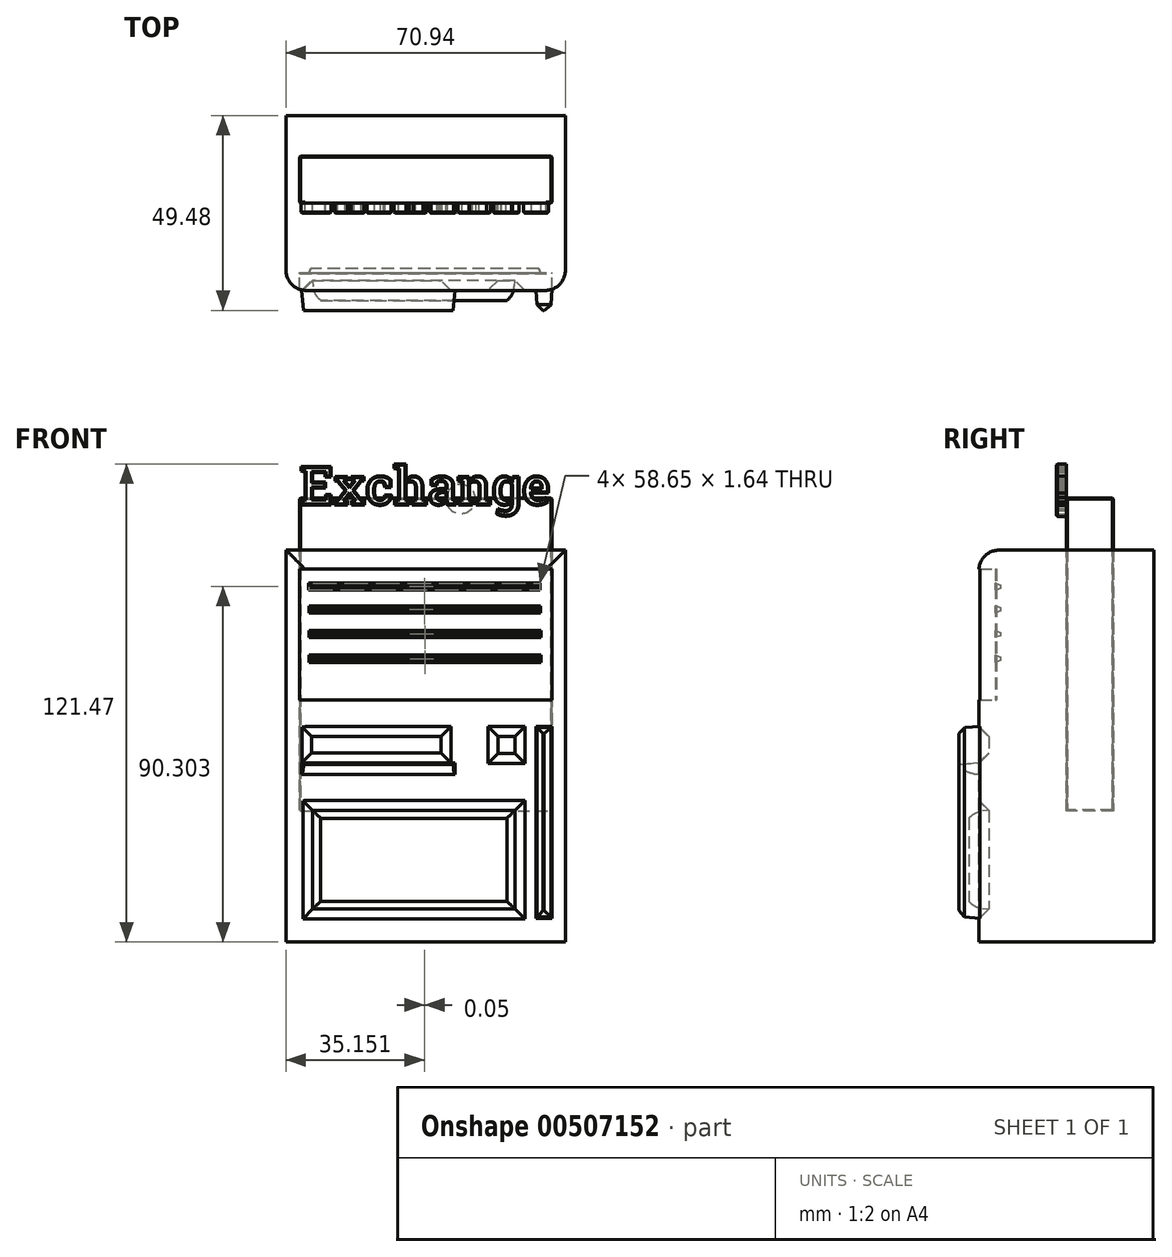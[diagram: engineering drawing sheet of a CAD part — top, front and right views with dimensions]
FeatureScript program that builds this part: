
annotation { "Feature Type Name" : "Feature", "Feature Type Description" : "" }
export const myFeature = defineFeature(function(context is Context, id is Id, definition is map)
    precondition{}
    {
        {
            var Q0;
            Q0=qCreatedBy(makeId("Top.planeOp"),FACE);
            var sketch = newSketch(context, id + "F0", { "sketchPlane" : qUnion([Q0])});
            skLineSegment(sketch, "E0.bottom", {"start": v(35.47, 22.2) * mm, "end": v(-35.47, 22.2) * mm});
            skLineSegment(sketch, "E0.top", {"start": v(35.47, -22.2) * mm, "end": v(-35.47, -22.2) * mm});
            skLineSegment(sketch, "E0.left", {"start": v(35.47, 22.2) * mm, "end": v(35.47, -22.2) * mm});
            skLineSegment(sketch, "E0.right", {"start": v(-35.47, 22.2) * mm, "end": v(-35.47, -22.2) * mm});
            skPoint(sketch, "E0.middle", {"position": v(0, 0) * mm});
            skLineSegment(sketch, "E1.bottom", {"start": v(-32.06, -22.2) * mm, "end": v(32.06, -22.2) * mm});
            skLineSegment(sketch, "E1.top", {"start": v(-32.06, -17.74) * mm, "end": v(32.06, -17.74) * mm});
            skLineSegment(sketch, "E1.left", {"start": v(-32.06, -22.2) * mm, "end": v(-32.06, -17.74) * mm});
            skLineSegment(sketch, "E1.right", {"start": v(32.06, -22.2) * mm, "end": v(32.06, -17.74) * mm});
            skLineSegment(sketch, "E2.bottom", {"start": v(32.06, -22.2) * mm, "end": v(-32.06, -22.2) * mm});
            skLineSegment(sketch, "E2.top", {"start": v(32.06, -31.14) * mm, "end": v(-32.06, -31.14) * mm});
            skLineSegment(sketch, "E2.left", {"start": v(32.06, -22.2) * mm, "end": v(32.06, -31.14) * mm});
            skLineSegment(sketch, "E2.right", {"start": v(-32.06, -22.2) * mm, "end": v(-32.06, -31.14) * mm});
            skLineSegment(sketch, "E3.bottom", {"start": v(-32.06, 22.2) * mm, "end": v(32.06, 22.2) * mm});
            skLineSegment(sketch, "E3.top", {"start": v(-32.06, 26.14) * mm, "end": v(32.06, 26.14) * mm});
            skLineSegment(sketch, "E3.left", {"start": v(-32.06, 22.2) * mm, "end": v(-32.06, 26.14) * mm});
            skLineSegment(sketch, "E3.right", {"start": v(32.06, 22.2) * mm, "end": v(32.06, 26.14) * mm});
            skLineSegment(sketch, "E4.bottom", {"start": v(-32.06, 0) * mm, "end": v(32.06, 0) * mm});
            skLineSegment(sketch, "E4.top", {"start": v(-32.06, 11.96) * mm, "end": v(32.06, 11.96) * mm});
            skLineSegment(sketch, "E4.left", {"start": v(-32.06, 0) * mm, "end": v(-32.06, 11.96) * mm});
            skLineSegment(sketch, "E4.right", {"start": v(32.06, 0) * mm, "end": v(32.06, 11.96) * mm});
            skSolve(sketch);
        }
        {
            var Q0;
            Q0=makeQuery(id+"F0.imprint","IMPRINT",FACE,{"disambiguationData":[TD([[makeQuery(id+"F0.imprint","IMPRINT",EDGE,{"derivedFrom":sQuery(id+"F0.wireOp",EDGE,"E4.bottom")}),1.0]])]});
            var Q1;
            {var subQ3=sQuery(id+"F0.wireOp",EDGE,"E0.left");Q1=makeQuery(id+"F0.imprint","IMPRINT",FACE,{"disambiguationData":[TD([[makeQuery(id+"F0.imprint","IMPRINT",EDGE,{"derivedFrom":subQ3}),-1.0]])]});}
            var Q2;
            Q2=makeQuery(id+"F0.imprint","IMPRINT",FACE,{"disambiguationData":[TD([[makeQuery(id+"F0.imprint","IMPRINT",EDGE,{"derivedFrom":sQuery(id+"F0.wireOp",EDGE,"E1.top")}),-1.0]])]});
            var Q3;
            Q3=makeQuery(id+"F0.imprint","IMPRINT",FACE,{"disambiguationData":[TD([[makeQuery(id+"F0.imprint","IMPRINT",EDGE,{"derivedFrom":sQuery(id+"F0.wireOp",EDGE,"E3.bottom")}),1.0]])]});
            extrude(context, id + "F1", {"entities" : qUnion([Q0, Q1, Q2, Q3]), "depth" : 99.57 * mm});
        }
        {
            var Q0;
            Q0=makeQuery(id+"F0.imprint","IMPRINT",FACE,{"disambiguationData":[TD([[makeQuery(id+"F0.imprint","IMPRINT",EDGE,{"derivedFrom":sQuery(id+"F0.wireOp",EDGE,"E1.top")}),-1.0]])]});
            extrude(context, id + "F2", {"entities" : qUnion([Q0]), "operationType" : NewBodyOperationType.REMOVE, "depth" : 94.74 * mm, "hasSecondDirection" : true, "secondDirectionOppositeDirection" : false, "secondDirectionDepth" : 61.47 * mm});
        }
        {
            var Q0;
            Q0=makeQuery(id+"F2.boolean.opBoolean","COPY",FACE,{"derivedFrom":makeQuery(id+"F2.opExtrude","SWEPT_FACE",FACE,{"disambiguationData":[OSD([sQuery(id+"F0.wireOp",EDGE,"E1.top")])]})});
            extrude(context, id + "F3", {"entities" : qUnion([Q0]), "depth" : 0.25 * mm});
        }
        {
            var Q0;
            Q0=makeQuery(id+"F0.imprint","IMPRINT",FACE,{"disambiguationData":[TD([[makeQuery(id+"F0.imprint","IMPRINT",EDGE,{"derivedFrom":sQuery(id+"F0.wireOp",EDGE,"E4.bottom")}),1.0]])]});
            extrude(context, id + "F4", {"entities" : qUnion([Q0]), "depth" : 112.78 * mm, "hasSecondDirection" : true, "secondDirectionOppositeDirection" : false, "secondDirectionDepth" : 33.27 * mm});
        }
        {
            var Q0;
            Q0=makeQuery(id+"F4.opExtrude","SWEPT_FACE",FACE,{"disambiguationData":[OSD([sQuery(id+"F0.wireOp",EDGE,"E4.bottom")])]});
            var sketch = newSketch(context, id + "F5", { "sketchPlane" : qUnion([Q0])});
            skText(sketch, "E5", { "text": "Exchange", "fontName": "RobotoSlab-Bold.ttf"});
            const initialGuessF5  = {"E5": [-0.03206, 0.11107, 1, 0, 0.00983]};
            skSetInitialGuess(sketch, initialGuessF5);
            skSolve(sketch);
        }
        {
            var Q0;
            Q0 = qSketchRegion(id + "F5", true);
            extrude(context, id + "F6", {"entities" : qUnion([Q0]), "operationType" : NewBodyOperationType.ADD, "depth" : 2.54 * mm});
        }
        {
            var Q0;
            Q0=makeQuery(id+"F6.opExtrude","CAP_FACE",FACE,{"disambiguationData":[OSD([sQuery(id+"F5.wireOp",EDGE,"E5.sketch_text.stroke-0"),sQuery(id+"F5.wireOp",EDGE,"E5.sketch_text.stroke-1"),sQuery(id+"F5.wireOp",EDGE,"E5.sketch_text.stroke-2"),sQuery(id+"F5.wireOp",EDGE,"E5.sketch_text.stroke-3"),sQuery(id+"F5.wireOp",EDGE,"E5.sketch_text.stroke-4"),sQuery(id+"F5.wireOp",EDGE,"E5.sketch_text.stroke-5"),sQuery(id+"F5.wireOp",EDGE,"E5.sketch_text.stroke-6"),sQuery(id+"F5.wireOp",EDGE,"E5.sketch_text.stroke-7"),sQuery(id+"F5.wireOp",EDGE,"E5.sketch_text.stroke-8"),sQuery(id+"F5.wireOp",EDGE,"E5.sketch_text.stroke-9"),sQuery(id+"F5.wireOp",EDGE,"E5.sketch_text.stroke-10"),sQuery(id+"F5.wireOp",EDGE,"E5.sketch_text.stroke-11"),sQuery(id+"F5.wireOp",EDGE,"E5.sketch_text.stroke-12"),sQuery(id+"F5.wireOp",EDGE,"E5.sketch_text.stroke-13"),sQuery(id+"F5.wireOp",EDGE,"E5.sketch_text.stroke-14"),sQuery(id+"F5.wireOp",EDGE,"E5.sketch_text.stroke-15"),sQuery(id+"F5.wireOp",EDGE,"E5.sketch_text.stroke-16"),sQuery(id+"F5.wireOp",EDGE,"E5.sketch_text.stroke-17"),sQuery(id+"F5.wireOp",EDGE,"E5.sketch_text.stroke-18"),sQuery(id+"F5.wireOp",EDGE,"E5.sketch_text.stroke-19"),sQuery(id+"F5.wireOp",EDGE,"E5.sketch_text.stroke-20")])],"isStart":false});
            var Q1;
            Q1=makeQuery(id+"F6.opExtrude","CAP_FACE",FACE,{"disambiguationData":[OSD([sQuery(id+"F5.wireOp",EDGE,"E5.sketch_text.stroke-21"),sQuery(id+"F5.wireOp",EDGE,"E5.sketch_text.stroke-22"),sQuery(id+"F5.wireOp",EDGE,"E5.sketch_text.stroke-23"),sQuery(id+"F5.wireOp",EDGE,"E5.sketch_text.stroke-24"),sQuery(id+"F5.wireOp",EDGE,"E5.sketch_text.stroke-25"),sQuery(id+"F5.wireOp",EDGE,"E5.sketch_text.stroke-26"),sQuery(id+"F5.wireOp",EDGE,"E5.sketch_text.stroke-27"),sQuery(id+"F5.wireOp",EDGE,"E5.sketch_text.stroke-28"),sQuery(id+"F5.wireOp",EDGE,"E5.sketch_text.stroke-29"),sQuery(id+"F5.wireOp",EDGE,"E5.sketch_text.stroke-30"),sQuery(id+"F5.wireOp",EDGE,"E5.sketch_text.stroke-31"),sQuery(id+"F5.wireOp",EDGE,"E5.sketch_text.stroke-32"),sQuery(id+"F5.wireOp",EDGE,"E5.sketch_text.stroke-33"),sQuery(id+"F5.wireOp",EDGE,"E5.sketch_text.stroke-34"),sQuery(id+"F5.wireOp",EDGE,"E5.sketch_text.stroke-35"),sQuery(id+"F5.wireOp",EDGE,"E5.sketch_text.stroke-36"),sQuery(id+"F5.wireOp",EDGE,"E5.sketch_text.stroke-37"),sQuery(id+"F5.wireOp",EDGE,"E5.sketch_text.stroke-38"),sQuery(id+"F5.wireOp",EDGE,"E5.sketch_text.stroke-39"),sQuery(id+"F5.wireOp",EDGE,"E5.sketch_text.stroke-40"),sQuery(id+"F5.wireOp",EDGE,"E5.sketch_text.stroke-41"),sQuery(id+"F5.wireOp",EDGE,"E5.sketch_text.stroke-42"),sQuery(id+"F5.wireOp",EDGE,"E5.sketch_text.stroke-43"),sQuery(id+"F5.wireOp",EDGE,"E5.sketch_text.stroke-44"),sQuery(id+"F5.wireOp",EDGE,"E5.sketch_text.stroke-45"),sQuery(id+"F5.wireOp",EDGE,"E5.sketch_text.stroke-46"),sQuery(id+"F5.wireOp",EDGE,"E5.sketch_text.stroke-47"),sQuery(id+"F5.wireOp",EDGE,"E5.sketch_text.stroke-48")])],"isStart":false});
            var Q2;
            Q2=makeQuery(id+"F6.opExtrude","CAP_FACE",FACE,{"disambiguationData":[OSD([sQuery(id+"F5.wireOp",EDGE,"E5.sketch_text.stroke-49"),sQuery(id+"F5.wireOp",EDGE,"E5.sketch_text.stroke-50"),sQuery(id+"F5.wireOp",EDGE,"E5.sketch_text.stroke-51"),sQuery(id+"F5.wireOp",EDGE,"E5.sketch_text.stroke-52"),sQuery(id+"F5.wireOp",EDGE,"E5.sketch_text.stroke-53"),sQuery(id+"F5.wireOp",EDGE,"E5.sketch_text.stroke-54"),sQuery(id+"F5.wireOp",EDGE,"E5.sketch_text.stroke-55"),sQuery(id+"F5.wireOp",EDGE,"E5.sketch_text.stroke-56"),sQuery(id+"F5.wireOp",EDGE,"E5.sketch_text.stroke-57"),sQuery(id+"F5.wireOp",EDGE,"E5.sketch_text.stroke-58"),sQuery(id+"F5.wireOp",EDGE,"E5.sketch_text.stroke-59"),sQuery(id+"F5.wireOp",EDGE,"E5.sketch_text.stroke-60"),sQuery(id+"F5.wireOp",EDGE,"E5.sketch_text.stroke-61"),sQuery(id+"F5.wireOp",EDGE,"E5.sketch_text.stroke-62"),sQuery(id+"F5.wireOp",EDGE,"E5.sketch_text.stroke-63"),sQuery(id+"F5.wireOp",EDGE,"E5.sketch_text.stroke-64"),sQuery(id+"F5.wireOp",EDGE,"E5.sketch_text.stroke-65"),sQuery(id+"F5.wireOp",EDGE,"E5.sketch_text.stroke-66"),sQuery(id+"F5.wireOp",EDGE,"E5.sketch_text.stroke-67"),sQuery(id+"F5.wireOp",EDGE,"E5.sketch_text.stroke-68"),sQuery(id+"F5.wireOp",EDGE,"E5.sketch_text.stroke-69"),sQuery(id+"F5.wireOp",EDGE,"E5.sketch_text.stroke-70"),sQuery(id+"F5.wireOp",EDGE,"E5.sketch_text.stroke-71")])],"isStart":false});
            var Q3;
            Q3=makeQuery(id+"F6.opExtrude","CAP_FACE",FACE,{"disambiguationData":[OSD([sQuery(id+"F5.wireOp",EDGE,"E5.sketch_text.stroke-72"),sQuery(id+"F5.wireOp",EDGE,"E5.sketch_text.stroke-73"),sQuery(id+"F5.wireOp",EDGE,"E5.sketch_text.stroke-74"),sQuery(id+"F5.wireOp",EDGE,"E5.sketch_text.stroke-75"),sQuery(id+"F5.wireOp",EDGE,"E5.sketch_text.stroke-76"),sQuery(id+"F5.wireOp",EDGE,"E5.sketch_text.stroke-77"),sQuery(id+"F5.wireOp",EDGE,"E5.sketch_text.stroke-78"),sQuery(id+"F5.wireOp",EDGE,"E5.sketch_text.stroke-79"),sQuery(id+"F5.wireOp",EDGE,"E5.sketch_text.stroke-80"),sQuery(id+"F5.wireOp",EDGE,"E5.sketch_text.stroke-81"),sQuery(id+"F5.wireOp",EDGE,"E5.sketch_text.stroke-82"),sQuery(id+"F5.wireOp",EDGE,"E5.sketch_text.stroke-83"),sQuery(id+"F5.wireOp",EDGE,"E5.sketch_text.stroke-84"),sQuery(id+"F5.wireOp",EDGE,"E5.sketch_text.stroke-85"),sQuery(id+"F5.wireOp",EDGE,"E5.sketch_text.stroke-86"),sQuery(id+"F5.wireOp",EDGE,"E5.sketch_text.stroke-87"),sQuery(id+"F5.wireOp",EDGE,"E5.sketch_text.stroke-88"),sQuery(id+"F5.wireOp",EDGE,"E5.sketch_text.stroke-89"),sQuery(id+"F5.wireOp",EDGE,"E5.sketch_text.stroke-90"),sQuery(id+"F5.wireOp",EDGE,"E5.sketch_text.stroke-91"),sQuery(id+"F5.wireOp",EDGE,"E5.sketch_text.stroke-92"),sQuery(id+"F5.wireOp",EDGE,"E5.sketch_text.stroke-93"),sQuery(id+"F5.wireOp",EDGE,"E5.sketch_text.stroke-94"),sQuery(id+"F5.wireOp",EDGE,"E5.sketch_text.stroke-95"),sQuery(id+"F5.wireOp",EDGE,"E5.sketch_text.stroke-96"),sQuery(id+"F5.wireOp",EDGE,"E5.sketch_text.stroke-97")])],"isStart":false});
            var Q4;
            Q4=makeQuery(id+"F6.opExtrude","CAP_FACE",FACE,{"disambiguationData":[OSD([sQuery(id+"F5.wireOp",EDGE,"E5.sketch_text.stroke-98"),sQuery(id+"F5.wireOp",EDGE,"E5.sketch_text.stroke-99"),sQuery(id+"F5.wireOp",EDGE,"E5.sketch_text.stroke-100"),sQuery(id+"F5.wireOp",EDGE,"E5.sketch_text.stroke-101"),sQuery(id+"F5.wireOp",EDGE,"E5.sketch_text.stroke-102"),sQuery(id+"F5.wireOp",EDGE,"E5.sketch_text.stroke-103"),sQuery(id+"F5.wireOp",EDGE,"E5.sketch_text.stroke-104"),sQuery(id+"F5.wireOp",EDGE,"E5.sketch_text.stroke-105"),sQuery(id+"F5.wireOp",EDGE,"E5.sketch_text.stroke-106"),sQuery(id+"F5.wireOp",EDGE,"E5.sketch_text.stroke-107"),sQuery(id+"F5.wireOp",EDGE,"E5.sketch_text.stroke-108"),sQuery(id+"F5.wireOp",EDGE,"E5.sketch_text.stroke-109"),sQuery(id+"F5.wireOp",EDGE,"E5.sketch_text.stroke-110"),sQuery(id+"F5.wireOp",EDGE,"E5.sketch_text.stroke-111"),sQuery(id+"F5.wireOp",EDGE,"E5.sketch_text.stroke-112"),sQuery(id+"F5.wireOp",EDGE,"E5.sketch_text.stroke-113"),sQuery(id+"F5.wireOp",EDGE,"E5.sketch_text.stroke-114"),sQuery(id+"F5.wireOp",EDGE,"E5.sketch_text.stroke-115"),sQuery(id+"F5.wireOp",EDGE,"E5.sketch_text.stroke-116"),sQuery(id+"F5.wireOp",EDGE,"E5.sketch_text.stroke-117"),sQuery(id+"F5.wireOp",EDGE,"E5.sketch_text.stroke-118"),sQuery(id+"F5.wireOp",EDGE,"E5.sketch_text.stroke-119"),sQuery(id+"F5.wireOp",EDGE,"E5.sketch_text.stroke-120"),sQuery(id+"F5.wireOp",EDGE,"E5.sketch_text.stroke-121"),sQuery(id+"F5.wireOp",EDGE,"E5.sketch_text.stroke-122"),sQuery(id+"F5.wireOp",EDGE,"E5.sketch_text.stroke-123"),sQuery(id+"F5.wireOp",EDGE,"E5.sketch_text.stroke-124"),sQuery(id+"F5.wireOp",EDGE,"E5.sketch_text.stroke-125"),sQuery(id+"F5.wireOp",EDGE,"E5.sketch_text.stroke-126"),sQuery(id+"F5.wireOp",EDGE,"E5.sketch_text.stroke-127"),sQuery(id+"F5.wireOp",EDGE,"E5.sketch_text.stroke-128"),sQuery(id+"F5.wireOp",EDGE,"E5.sketch_text.stroke-129"),sQuery(id+"F5.wireOp",EDGE,"E5.sketch_text.stroke-130"),sQuery(id+"F5.wireOp",EDGE,"E5.sketch_text.stroke-131"),sQuery(id+"F5.wireOp",EDGE,"E5.sketch_text.stroke-132")])],"isStart":false});
            var Q5;
            Q5=makeQuery(id+"F6.opExtrude","CAP_FACE",FACE,{"disambiguationData":[OSD([sQuery(id+"F5.wireOp",EDGE,"E5.sketch_text.stroke-133"),sQuery(id+"F5.wireOp",EDGE,"E5.sketch_text.stroke-134"),sQuery(id+"F5.wireOp",EDGE,"E5.sketch_text.stroke-135"),sQuery(id+"F5.wireOp",EDGE,"E5.sketch_text.stroke-136"),sQuery(id+"F5.wireOp",EDGE,"E5.sketch_text.stroke-137"),sQuery(id+"F5.wireOp",EDGE,"E5.sketch_text.stroke-138"),sQuery(id+"F5.wireOp",EDGE,"E5.sketch_text.stroke-139"),sQuery(id+"F5.wireOp",EDGE,"E5.sketch_text.stroke-140"),sQuery(id+"F5.wireOp",EDGE,"E5.sketch_text.stroke-141"),sQuery(id+"F5.wireOp",EDGE,"E5.sketch_text.stroke-142"),sQuery(id+"F5.wireOp",EDGE,"E5.sketch_text.stroke-143"),sQuery(id+"F5.wireOp",EDGE,"E5.sketch_text.stroke-144"),sQuery(id+"F5.wireOp",EDGE,"E5.sketch_text.stroke-145"),sQuery(id+"F5.wireOp",EDGE,"E5.sketch_text.stroke-146"),sQuery(id+"F5.wireOp",EDGE,"E5.sketch_text.stroke-147"),sQuery(id+"F5.wireOp",EDGE,"E5.sketch_text.stroke-148"),sQuery(id+"F5.wireOp",EDGE,"E5.sketch_text.stroke-149"),sQuery(id+"F5.wireOp",EDGE,"E5.sketch_text.stroke-150"),sQuery(id+"F5.wireOp",EDGE,"E5.sketch_text.stroke-151"),sQuery(id+"F5.wireOp",EDGE,"E5.sketch_text.stroke-152"),sQuery(id+"F5.wireOp",EDGE,"E5.sketch_text.stroke-153"),sQuery(id+"F5.wireOp",EDGE,"E5.sketch_text.stroke-154"),sQuery(id+"F5.wireOp",EDGE,"E5.sketch_text.stroke-155"),sQuery(id+"F5.wireOp",EDGE,"E5.sketch_text.stroke-156"),sQuery(id+"F5.wireOp",EDGE,"E5.sketch_text.stroke-157"),sQuery(id+"F5.wireOp",EDGE,"E5.sketch_text.stroke-158")])],"isStart":false});
            var Q6;
            Q6=makeQuery(id+"F6.opExtrude","CAP_FACE",FACE,{"disambiguationData":[OSD([sQuery(id+"F5.wireOp",EDGE,"E5.sketch_text.stroke-159"),sQuery(id+"F5.wireOp",EDGE,"E5.sketch_text.stroke-160"),sQuery(id+"F5.wireOp",EDGE,"E5.sketch_text.stroke-161"),sQuery(id+"F5.wireOp",EDGE,"E5.sketch_text.stroke-162"),sQuery(id+"F5.wireOp",EDGE,"E5.sketch_text.stroke-163"),sQuery(id+"F5.wireOp",EDGE,"E5.sketch_text.stroke-164"),sQuery(id+"F5.wireOp",EDGE,"E5.sketch_text.stroke-165"),sQuery(id+"F5.wireOp",EDGE,"E5.sketch_text.stroke-166"),sQuery(id+"F5.wireOp",EDGE,"E5.sketch_text.stroke-167"),sQuery(id+"F5.wireOp",EDGE,"E5.sketch_text.stroke-168"),sQuery(id+"F5.wireOp",EDGE,"E5.sketch_text.stroke-169"),sQuery(id+"F5.wireOp",EDGE,"E5.sketch_text.stroke-170"),sQuery(id+"F5.wireOp",EDGE,"E5.sketch_text.stroke-171"),sQuery(id+"F5.wireOp",EDGE,"E5.sketch_text.stroke-172"),sQuery(id+"F5.wireOp",EDGE,"E5.sketch_text.stroke-173"),sQuery(id+"F5.wireOp",EDGE,"E5.sketch_text.stroke-174"),sQuery(id+"F5.wireOp",EDGE,"E5.sketch_text.stroke-175"),sQuery(id+"F5.wireOp",EDGE,"E5.sketch_text.stroke-176"),sQuery(id+"F5.wireOp",EDGE,"E5.sketch_text.stroke-177"),sQuery(id+"F5.wireOp",EDGE,"E5.sketch_text.stroke-178"),sQuery(id+"F5.wireOp",EDGE,"E5.sketch_text.stroke-179"),sQuery(id+"F5.wireOp",EDGE,"E5.sketch_text.stroke-180"),sQuery(id+"F5.wireOp",EDGE,"E5.sketch_text.stroke-181"),sQuery(id+"F5.wireOp",EDGE,"E5.sketch_text.stroke-182"),sQuery(id+"F5.wireOp",EDGE,"E5.sketch_text.stroke-183"),sQuery(id+"F5.wireOp",EDGE,"E5.sketch_text.stroke-184"),sQuery(id+"F5.wireOp",EDGE,"E5.sketch_text.stroke-185"),sQuery(id+"F5.wireOp",EDGE,"E5.sketch_text.stroke-186"),sQuery(id+"F5.wireOp",EDGE,"E5.sketch_text.stroke-187"),sQuery(id+"F5.wireOp",EDGE,"E5.sketch_text.stroke-188"),sQuery(id+"F5.wireOp",EDGE,"E5.sketch_text.stroke-189"),sQuery(id+"F5.wireOp",EDGE,"E5.sketch_text.stroke-190")])],"isStart":false});
            var Q7;
            Q7=makeQuery(id+"F6.opExtrude","CAP_FACE",FACE,{"disambiguationData":[OSD([sQuery(id+"F5.wireOp",EDGE,"E5.sketch_text.stroke-191"),sQuery(id+"F5.wireOp",EDGE,"E5.sketch_text.stroke-192"),sQuery(id+"F5.wireOp",EDGE,"E5.sketch_text.stroke-193"),sQuery(id+"F5.wireOp",EDGE,"E5.sketch_text.stroke-194"),sQuery(id+"F5.wireOp",EDGE,"E5.sketch_text.stroke-195"),sQuery(id+"F5.wireOp",EDGE,"E5.sketch_text.stroke-196"),sQuery(id+"F5.wireOp",EDGE,"E5.sketch_text.stroke-197"),sQuery(id+"F5.wireOp",EDGE,"E5.sketch_text.stroke-198"),sQuery(id+"F5.wireOp",EDGE,"E5.sketch_text.stroke-199"),sQuery(id+"F5.wireOp",EDGE,"E5.sketch_text.stroke-200"),sQuery(id+"F5.wireOp",EDGE,"E5.sketch_text.stroke-201"),sQuery(id+"F5.wireOp",EDGE,"E5.sketch_text.stroke-202"),sQuery(id+"F5.wireOp",EDGE,"E5.sketch_text.stroke-203"),sQuery(id+"F5.wireOp",EDGE,"E5.sketch_text.stroke-204"),sQuery(id+"F5.wireOp",EDGE,"E5.sketch_text.stroke-205"),sQuery(id+"F5.wireOp",EDGE,"E5.sketch_text.stroke-206"),sQuery(id+"F5.wireOp",EDGE,"E5.sketch_text.stroke-207"),sQuery(id+"F5.wireOp",EDGE,"E5.sketch_text.stroke-208"),sQuery(id+"F5.wireOp",EDGE,"E5.sketch_text.stroke-209"),sQuery(id+"F5.wireOp",EDGE,"E5.sketch_text.stroke-210"),sQuery(id+"F5.wireOp",EDGE,"E5.sketch_text.stroke-211"),sQuery(id+"F5.wireOp",EDGE,"E5.sketch_text.stroke-212"),sQuery(id+"F5.wireOp",EDGE,"E5.sketch_text.stroke-213"),sQuery(id+"F5.wireOp",EDGE,"E5.sketch_text.stroke-214")])],"isStart":false});
            var Q8;
            Q8=makeQuery(id+"F4.opExtrude","SWEPT_FACE",FACE,{"disambiguationData":[OSD([sQuery(id+"F0.wireOp",EDGE,"E4.left")])]});
            var Q9;
            Q9=makeQuery(id+"F4.opExtrude","SWEPT_FACE",FACE,{"disambiguationData":[OSD([sQuery(id+"F0.wireOp",EDGE,"E4.right")])]});
            var Q10;
            Q10=makeQuery(id+"F4.opExtrude","CAP_EDGE",EDGE,{"disambiguationData":[OSD([sQuery(id+"F0.wireOp",EDGE,"E4.top")])],"isStart":false});
            var Q11;
            {var subQ1=sQuery(id+"F0.wireOp",EDGE,"E4.right");var subQ2=sQuery(id+"F0.wireOp",EDGE,"E4.bottom");var subQ3=makeQuery(id+"F4.opExtrude","CAP_FACE",FACE,{"disambiguationData":[OSD([subQ2,sQuery(id+"F0.wireOp",EDGE,"E4.top"),sQuery(id+"F0.wireOp",EDGE,"E4.left"),subQ1])],"isStart":false});var subQ4=makeQuery(id+"F4.opExtrude","SWEPT_FACE",FACE,{"disambiguationData":[OSD([subQ2])]});Q11=makeQuery(id+"F6.boolean.opBoolean","SPLIT",EDGE,{"disambiguationData":[topologyDisambiguationEdgeConnected([subQ4,subQ3]),TD([makeQuery(id+"F4.opExtrude","SWEPT_FACE",FACE,{"disambiguationData":[OSD([subQ1])]})])],"derivedFrom":makeQuery(id+"F4.opExtrude","CAP_EDGE",EDGE,{"disambiguationData":[OSD([subQ2])],"isStart":false})});}
            var Q12;
            {var subQ1=sQuery(id+"F0.wireOp",EDGE,"E4.left");var subQ2=sQuery(id+"F0.wireOp",EDGE,"E4.bottom");var subQ3=makeQuery(id+"F4.opExtrude","CAP_FACE",FACE,{"disambiguationData":[OSD([subQ2,sQuery(id+"F0.wireOp",EDGE,"E4.top"),subQ1,sQuery(id+"F0.wireOp",EDGE,"E4.right")])],"isStart":false});var subQ4=makeQuery(id+"F4.opExtrude","SWEPT_FACE",FACE,{"disambiguationData":[OSD([subQ2])]});Q12=makeQuery(id+"F6.boolean.opBoolean","SPLIT",EDGE,{"disambiguationData":[topologyDisambiguationEdgeConnected([subQ4,subQ3]),TD([makeQuery(id+"F4.opExtrude","SWEPT_FACE",FACE,{"disambiguationData":[OSD([subQ1])]})])],"derivedFrom":makeQuery(id+"F4.opExtrude","CAP_EDGE",EDGE,{"disambiguationData":[OSD([subQ2])],"isStart":false})});}
            chamfer(context, id + "F7", {"entities" : qUnion([Q0, Q1, Q2, Q3, Q4, Q5, Q6, Q7, Q8, Q9, Q10, Q11, Q12]), "chamferType" : ChamferType.OFFSET_ANGLE, "width" : 0.25 * mm, "oppositeDirection" : false, "angle" : 45 * degree, "tangentPropagation" : true});
        }
        {
            var Q0;
            Q0=makeQuery(id+"F3.opExtrude","CAP_FACE",FACE,{"disambiguationData":[OSD([sQuery(id+"F0.wireOp",EDGE,"E1.top")])],"isStart":false});
            var sketch = newSketch(context, id + "F8", { "sketchPlane" : qUnion([Q0])});
            skLineSegment(sketch, "E6.bottom", {"start": v(-29.74, 91.21) * mm, "end": v(29.1, 91.21) * mm});
            skLineSegment(sketch, "E6.top", {"start": v(-29.74, 89.4) * mm, "end": v(29.1, 89.4) * mm});
            skLineSegment(sketch, "E6.left", {"start": v(-29.74, 91.21) * mm, "end": v(-29.74, 89.4) * mm});
            skLineSegment(sketch, "E6.right", {"start": v(29.1, 91.21) * mm, "end": v(29.1, 89.4) * mm});
            skLineSegment(sketch, "E7.bottom", {"start": v(-29.69, 85.42) * mm, "end": v(29.15, 85.42) * mm});
            skLineSegment(sketch, "E7.top", {"start": v(-29.69, 83.6) * mm, "end": v(29.15, 83.6) * mm});
            skLineSegment(sketch, "E7.left", {"start": v(-29.69, 85.42) * mm, "end": v(-29.69, 83.6) * mm});
            skLineSegment(sketch, "E7.right", {"start": v(29.15, 85.42) * mm, "end": v(29.15, 83.6) * mm});
            skLineSegment(sketch, "E8.bottom", {"start": v(-29.6, 79.16) * mm, "end": v(29.25, 79.16) * mm});
            skLineSegment(sketch, "E8.top", {"start": v(-29.6, 77.33) * mm, "end": v(29.25, 77.33) * mm});
            skLineSegment(sketch, "E8.left", {"start": v(-29.6, 79.16) * mm, "end": v(-29.6, 77.33) * mm});
            skLineSegment(sketch, "E8.right", {"start": v(29.25, 79.16) * mm, "end": v(29.25, 77.33) * mm});
            skLineSegment(sketch, "E9.bottom", {"start": v(-29.6, 72.86) * mm, "end": v(29.25, 72.86) * mm});
            skLineSegment(sketch, "E9.top", {"start": v(-29.6, 71.04) * mm, "end": v(29.25, 71.04) * mm});
            skLineSegment(sketch, "E9.left", {"start": v(-29.6, 72.86) * mm, "end": v(-29.6, 71.04) * mm});
            skLineSegment(sketch, "E9.right", {"start": v(29.25, 72.86) * mm, "end": v(29.25, 71.04) * mm});
            skSolve(sketch);
        }
        {
            var Q0;
            Q0=makeQuery(id+"F8.imprint","IMPRINT",FACE,{"disambiguationData":[TD([[makeQuery(id+"F8.imprint","IMPRINT",EDGE,{"derivedFrom":sQuery(id+"F8.wireOp",EDGE,"E9.bottom")}),-1.0]])]});
            var Q1;
            Q1=makeQuery(id+"F8.imprint","IMPRINT",FACE,{"disambiguationData":[TD([[makeQuery(id+"F8.imprint","IMPRINT",EDGE,{"derivedFrom":sQuery(id+"F8.wireOp",EDGE,"E8.bottom")}),-1.0]])]});
            var Q2;
            Q2=makeQuery(id+"F8.imprint","IMPRINT",FACE,{"disambiguationData":[TD([[makeQuery(id+"F8.imprint","IMPRINT",EDGE,{"derivedFrom":sQuery(id+"F8.wireOp",EDGE,"E7.bottom")}),-1.0]])]});
            var Q3;
            Q3=makeQuery(id+"F8.imprint","IMPRINT",FACE,{"disambiguationData":[TD([[makeQuery(id+"F8.imprint","IMPRINT",EDGE,{"derivedFrom":sQuery(id+"F8.wireOp",EDGE,"E6.bottom")}),-1.0]])]});
            extrude(context, id + "F9", {"entities" : qUnion([Q0, Q1, Q2, Q3]), "operationType" : NewBodyOperationType.REMOVE, "oppositeDirection" : true, "depth" : 1.27 * mm, "hasDraft" : true, "draftAngle" : 20 * degree, "draftPullDirection" : true});
        }
        {
            var Q0;
            Q0=makeQuery(id+"F1.opExtrude","SWEPT_FACE",FACE,{"disambiguationData":[OSD([sQuery(id+"F0.wireOp",EDGE,"E0.top"),sQuery(id+"F0.wireOp",EDGE,"E2.bottom")])]});
            var sketch = newSketch(context, id + "F10", { "sketchPlane" : qUnion([Q0])});
            skLineSegment(sketch, "E10.bottom", {"start": v(-31.49, 54.7) * mm, "end": v(6.4, 54.7) * mm});
            skLineSegment(sketch, "E10.top", {"start": v(-31.49, 45.53) * mm, "end": v(6.4, 45.53) * mm});
            skLineSegment(sketch, "E10.left", {"start": v(-31.49, 54.7) * mm, "end": v(-31.49, 45.53) * mm});
            skLineSegment(sketch, "E10.right", {"start": v(6.4, 54.7) * mm, "end": v(6.4, 45.53) * mm});
            skLineSegment(sketch, "E11.bottom", {"start": v(15.86, 54.72) * mm, "end": v(25.18, 54.72) * mm});
            skLineSegment(sketch, "E11.top", {"start": v(15.86, 45.35) * mm, "end": v(25.18, 45.35) * mm});
            skLineSegment(sketch, "E11.left", {"start": v(15.86, 54.72) * mm, "end": v(15.86, 45.35) * mm});
            skLineSegment(sketch, "E11.right", {"start": v(25.18, 54.72) * mm, "end": v(25.18, 45.35) * mm});
            skLineSegment(sketch, "E12.bottom", {"start": v(25.18, 45.35) * mm, "end": v(15.86, 45.35) * mm});
            skLineSegment(sketch, "E12.top", {"start": v(25.18, 42.6) * mm, "end": v(15.86, 42.6) * mm});
            skLineSegment(sketch, "E12.left", {"start": v(25.18, 45.35) * mm, "end": v(25.18, 42.6) * mm});
            skLineSegment(sketch, "E12.right", {"start": v(15.86, 45.35) * mm, "end": v(15.86, 42.6) * mm});
            skLineSegment(sketch, "E13.bottom", {"start": v(-31.24, 35.93) * mm, "end": v(25.18, 35.93) * mm});
            skLineSegment(sketch, "E13.top", {"start": v(-31.24, 5.84) * mm, "end": v(25.18, 5.84) * mm});
            skLineSegment(sketch, "E13.left", {"start": v(-31.24, 35.93) * mm, "end": v(-31.24, 5.84) * mm});
            skLineSegment(sketch, "E13.right", {"start": v(25.18, 35.93) * mm, "end": v(25.18, 5.84) * mm});
            skLineSegment(sketch, "E14.bottom", {"start": v(32.1, 54.79) * mm, "end": v(28.01, 54.79) * mm});
            skLineSegment(sketch, "E14.top", {"start": v(32.1, 5.99) * mm, "end": v(28.01, 5.99) * mm});
            skLineSegment(sketch, "E14.left", {"start": v(32.1, 54.79) * mm, "end": v(32.1, 5.99) * mm});
            skLineSegment(sketch, "E14.right", {"start": v(28.01, 54.79) * mm, "end": v(28.01, 5.99) * mm});
            skLineSegment(sketch, "E15.bottom", {"start": v(-31.49, 45.53) * mm, "end": v(7.43, 45.53) * mm});
            skLineSegment(sketch, "E15.top", {"start": v(-31.49, 42.6) * mm, "end": v(7.43, 42.6) * mm});
            skLineSegment(sketch, "E15.left", {"start": v(-31.49, 45.53) * mm, "end": v(-31.49, 42.6) * mm});
            skLineSegment(sketch, "E15.right", {"start": v(7.43, 45.53) * mm, "end": v(7.43, 42.6) * mm});
            skSolve(sketch);
        }
        {
            var Q0;
            Q0=makeQuery(id+"F10.imprint","IMPRINT",FACE,{"disambiguationData":[TD([[makeQuery(id+"F10.imprint","IMPRINT",EDGE,{"derivedFrom":sQuery(id+"F10.wireOp",EDGE,"E10.bottom")}),-1.0]])]});
            var Q1;
            Q1=makeQuery(id+"F10.imprint","IMPRINT",FACE,{"disambiguationData":[TD([[makeQuery(id+"F10.imprint","IMPRINT",EDGE,{"derivedFrom":sQuery(id+"F10.wireOp",EDGE,"E11.bottom")}),-1.0]])]});
            var Q2;
            Q2=makeQuery(id+"F10.imprint","IMPRINT",FACE,{"disambiguationData":[TD([[makeQuery(id+"F10.imprint","IMPRINT",EDGE,{"derivedFrom":sQuery(id+"F10.wireOp",EDGE,"E13.bottom")}),-1.0]])]});
            extrude(context, id + "F11", {"entities" : qUnion([Q0, Q1, Q2]), "operationType" : NewBodyOperationType.REMOVE, "oppositeDirection" : true, "depth" : 2.54 * mm, "hasDraft" : true, "draftAngle" : 45 * degree, "draftPullDirection" : true});
        }
        {
            var Q0;
            Q0=makeQuery(id+"F10.imprint","IMPRINT",FACE,{"disambiguationData":[TD([[makeQuery(id+"F10.imprint","IMPRINT",EDGE,{"derivedFrom":sQuery(id+"F10.wireOp",EDGE,"E15.top")}),1.0]])]});
            var Q1;
            Q1=makeQuery(id+"F10.imprint","IMPRINT",FACE,{"disambiguationData":[TD([[makeQuery(id+"F10.imprint","IMPRINT",EDGE,{"derivedFrom":sQuery(id+"F10.wireOp",EDGE,"E12.bottom")}),1.0]])]});
            var Q2;
            Q2=makeQuery(id+"F10.imprint","IMPRINT",FACE,{"disambiguationData":[TD([[makeQuery(id+"F10.imprint","IMPRINT",EDGE,{"derivedFrom":sQuery(id+"F10.wireOp",EDGE,"E14.bottom")}),1.0]])]});
            var Q3;
            Q3=makeQuery(id+"F11.boolean.opBoolean","COPY",FACE,{"derivedFrom":makeQuery(id+"F11.opExtrude","CAP_FACE",FACE,{"disambiguationData":[OSD([sQuery(id+"F10.wireOp",EDGE,"E13.bottom"),sQuery(id+"F10.wireOp",EDGE,"E13.top"),sQuery(id+"F10.wireOp",EDGE,"E13.left"),sQuery(id+"F10.wireOp",EDGE,"E13.right")])],"isStart":false})});
            extrude(context, id + "F12", {"entities" : qUnion([Q0, Q1, Q2, Q3]), "operationType" : NewBodyOperationType.ADD, "depth" : 5.08 * mm, "hasDraft" : true, "draftAngle" : 5 * degree, "draftPullDirection" : true});
        }
        {
            var Q0;
            Q0=makeQuery(id+"F12.opExtrude","CAP_FACE",FACE,{"disambiguationData":[OSD([sQuery(id+"F10.wireOp",EDGE,"E13.bottom"),sQuery(id+"F10.wireOp",EDGE,"E13.top"),sQuery(id+"F10.wireOp",EDGE,"E13.left"),sQuery(id+"F10.wireOp",EDGE,"E13.right")])],"isStart":false});
            var Q1;
            Q1=makeQuery(id+"F12.opExtrude","CAP_FACE",FACE,{"disambiguationData":[OSD([sQuery(id+"F10.wireOp",EDGE,"E14.bottom"),sQuery(id+"F10.wireOp",EDGE,"E14.top"),sQuery(id+"F10.wireOp",EDGE,"E14.left"),sQuery(id+"F10.wireOp",EDGE,"E14.right")])],"isStart":false});
            chamfer(context, id + "F13", {"entities" : qUnion([Q0, Q1]), "chamferType" : ChamferType.OFFSET_ANGLE, "width" : 1.4 * mm, "oppositeDirection" : false, "angle" : 45 * degree, "tangentPropagation" : true});
        }
        {
            var Q0;
            Q0=makeQuery(id+"F11.boolean.opBoolean","COPY",EDGE,{"derivedFrom":makeQuery(id+"F11.opExtrude","CAP_EDGE",EDGE,{"disambiguationData":[OSD([sQuery(id+"F10.wireOp",EDGE,"E13.bottom")])],"isStart":true})});
            var Q1;
            Q1=makeQuery(id+"F11.boolean.opBoolean","COPY",EDGE,{"derivedFrom":makeQuery(id+"F11.opExtrude","CAP_EDGE",EDGE,{"disambiguationData":[OSD([sQuery(id+"F10.wireOp",EDGE,"E13.left")])],"isStart":true})});
            var Q2;
            Q2=makeQuery(id+"F11.boolean.opBoolean","COPY",EDGE,{"derivedFrom":makeQuery(id+"F11.opExtrude","CAP_EDGE",EDGE,{"disambiguationData":[OSD([sQuery(id+"F10.wireOp",EDGE,"E13.top")])],"isStart":true})});
            var Q3;
            Q3=makeQuery(id+"F11.boolean.opBoolean","COPY",EDGE,{"derivedFrom":makeQuery(id+"F11.opExtrude","CAP_EDGE",EDGE,{"disambiguationData":[OSD([sQuery(id+"F10.wireOp",EDGE,"E13.right")])],"isStart":true})});
            var Q4;
            {var subQ0=sQuery(id+"F10.wireOp",EDGE,"E13.left");Q4=makeQuery(id+"F13.opChamfer","BLEND_EDGE",EDGE,{"blendedFrom":[makeQuery(id+"F12.opExtrude","CAP_EDGE",EDGE,{"disambiguationData":[OSD([subQ0])],"isStart":false}),makeQuery(id+"F12.opExtrude","SWEPT_FACE",FACE,{"disambiguationData":[OSD([subQ0])]})],"blendedInto":[makeQuery(id+"F12.opExtrude","SWEPT_FACE",FACE,{"disambiguationData":[OSD([subQ0])]})]});}
            var Q5;
            {var subQ0=sQuery(id+"F10.wireOp",EDGE,"E13.bottom");Q5=makeQuery(id+"F13.opChamfer","BLEND_EDGE",EDGE,{"blendedFrom":[makeQuery(id+"F12.opExtrude","CAP_EDGE",EDGE,{"disambiguationData":[OSD([subQ0])],"isStart":false}),makeQuery(id+"F12.opExtrude","SWEPT_FACE",FACE,{"disambiguationData":[OSD([subQ0])]})],"blendedInto":[makeQuery(id+"F12.opExtrude","SWEPT_FACE",FACE,{"disambiguationData":[OSD([subQ0])]})]});}
            var Q6;
            {var subQ0=sQuery(id+"F10.wireOp",EDGE,"E13.right");Q6=makeQuery(id+"F13.opChamfer","BLEND_EDGE",EDGE,{"blendedFrom":[makeQuery(id+"F12.opExtrude","CAP_EDGE",EDGE,{"disambiguationData":[OSD([subQ0])],"isStart":false}),makeQuery(id+"F12.opExtrude","SWEPT_FACE",FACE,{"disambiguationData":[OSD([subQ0])]})],"blendedInto":[makeQuery(id+"F12.opExtrude","SWEPT_FACE",FACE,{"disambiguationData":[OSD([subQ0])]})]});}
            var Q7;
            {var subQ0=sQuery(id+"F10.wireOp",EDGE,"E13.top");Q7=makeQuery(id+"F13.opChamfer","BLEND_EDGE",EDGE,{"blendedFrom":[makeQuery(id+"F12.opExtrude","CAP_EDGE",EDGE,{"disambiguationData":[OSD([subQ0])],"isStart":false}),makeQuery(id+"F12.opExtrude","SWEPT_FACE",FACE,{"disambiguationData":[OSD([subQ0])]})],"blendedInto":[makeQuery(id+"F12.opExtrude","SWEPT_FACE",FACE,{"disambiguationData":[OSD([subQ0])]})]});}
            var Q8;
            Q8=makeQuery(id+"F12.opExtrude","CAP_EDGE",EDGE,{"disambiguationData":[OSD([sQuery(id+"F10.wireOp",EDGE,"E15.top")])],"isStart":false});
            var Q9;
            Q9=makeQuery(id+"F12.opExtrude","CAP_EDGE",EDGE,{"disambiguationData":[OSD([sQuery(id+"F10.wireOp",EDGE,"E12.top")])],"isStart":false});
            var Q10;
            Q10=makeQuery(id+"F1.opExtrude","SWEPT_EDGE",EDGE,{"disambiguationData":[OSD([sQuery(id+"F0.wireOp",EDGE,"E3.top"),sQuery(id+"F0.wireOp",EDGE,"E3.left")])]});
            var Q11;
            Q11=makeQuery(id+"F1.opExtrude","SWEPT_EDGE",EDGE,{"disambiguationData":[OSD([sQuery(id+"F0.wireOp",EDGE,"E3.top"),sQuery(id+"F0.wireOp",EDGE,"E3.right")])]});
            var Q12;
            Q12=makeQuery(id+"F1.opExtrude","CAP_EDGE",EDGE,{"disambiguationData":[OSD([sQuery(id+"F0.wireOp",EDGE,"E0.top"),sQuery(id+"F0.wireOp",EDGE,"E2.bottom")])],"isStart":false});
            var Q13;
            Q13=makeQuery(id+"F1.opExtrude","SWEPT_EDGE",EDGE,{"disambiguationData":[OSD([sQuery(id+"F0.wireOp",EDGE,"E0.top"),sQuery(id+"F0.wireOp",EDGE,"E0.right")])]});
            var Q14;
            Q14=makeQuery(id+"F1.opExtrude","SWEPT_EDGE",EDGE,{"disambiguationData":[OSD([sQuery(id+"F0.wireOp",EDGE,"E0.top"),sQuery(id+"F0.wireOp",EDGE,"E0.left")])]});
            fillet(context, id + "F14", {"entities" : qUnion([Q0, Q1, Q2, Q3, Q4, Q5, Q6, Q7, Q8, Q9, Q10, Q11, Q12, Q13, Q14]), "radius" : 5.08 * mm, "tangentPropagation" : true, "allowEdgeOverflow" : false});
        }
    });
